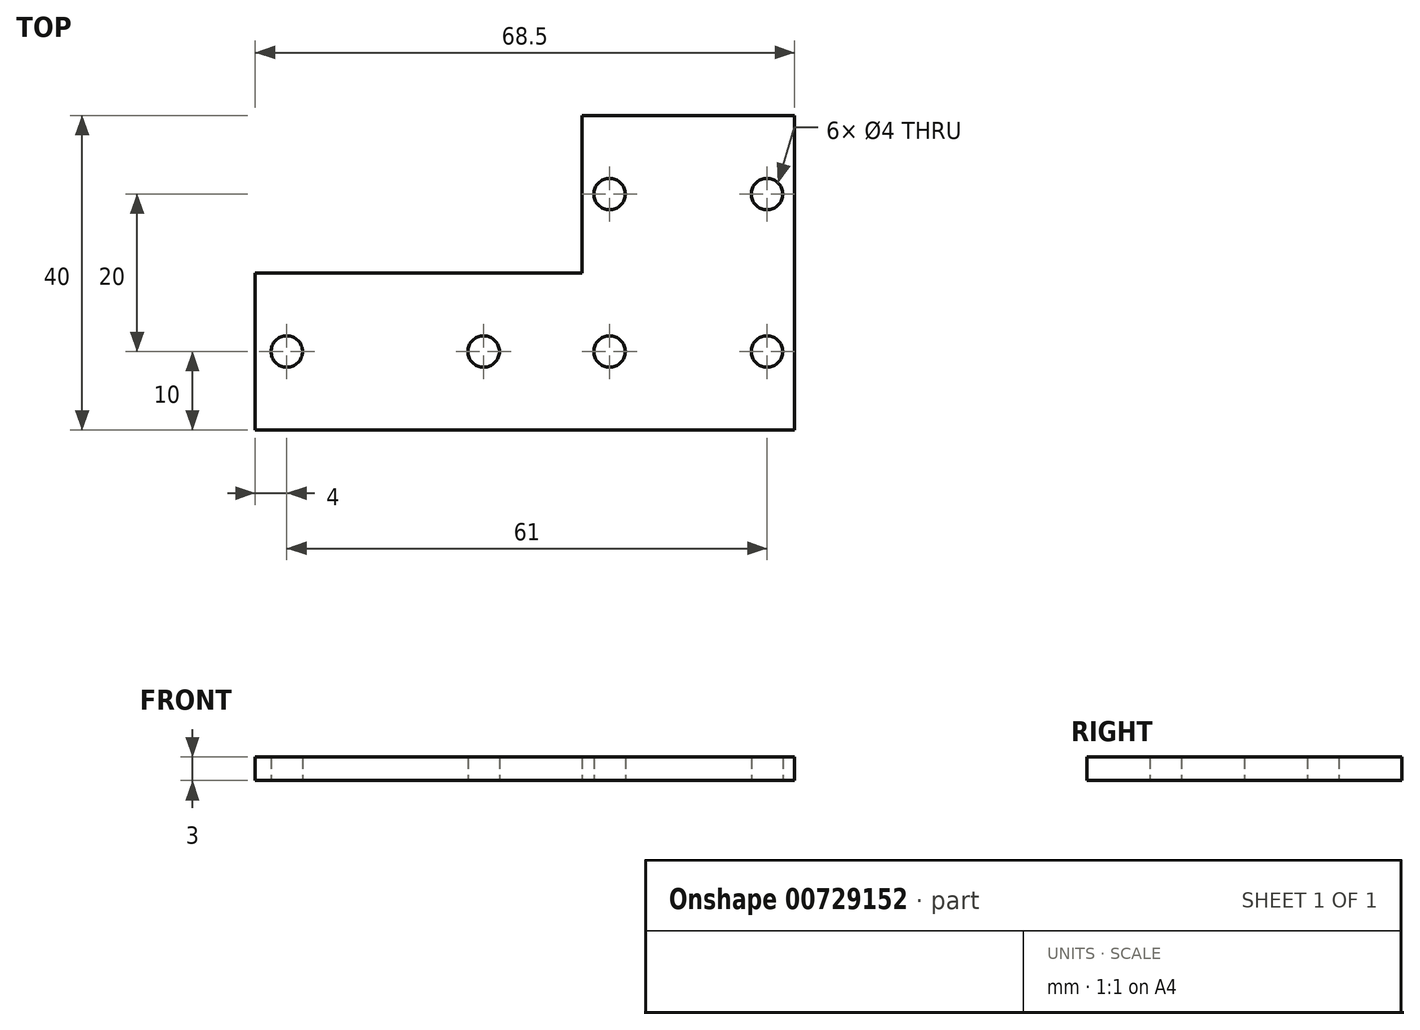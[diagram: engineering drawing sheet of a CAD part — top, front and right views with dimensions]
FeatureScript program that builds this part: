
annotation { "Feature Type Name" : "Feature", "Feature Type Description" : "" }
export const myFeature = defineFeature(function(context is Context, id is Id, definition is map)
    precondition{}
    {
        {
            var Q0;
            Q0=qCreatedBy(makeId("Top.planeOp"),FACE);
            var sketch = newSketch(context, id + "F0", { "sketchPlane" : qUnion([Q0])});
            skLineSegment(sketch, "E0.bottom", {"start": v(13.5, -20) * mm, "end": v(-55, -20) * mm});
            skLineSegment(sketch, "E0.top", {"start": v(13.5, 20) * mm, "end": v(-55, 20) * mm});
            skLineSegment(sketch, "E0.left", {"start": v(13.5, -20) * mm, "end": v(13.5, 20) * mm});
            skLineSegment(sketch, "E0.right", {"start": v(-55, -20) * mm, "end": v(-55, 20) * mm});
            skPoint(sketch, "E0.middle", {"position": v(0, 0) * mm});
            skLineSegment(sketch, "E1.bottom", {"start": v(10, -10) * mm, "end": v(-10, -10) * mm, "construction": true});
            skLineSegment(sketch, "E1.top", {"start": v(10, 10) * mm, "end": v(-10, 10) * mm, "construction": true});
            skLineSegment(sketch, "E1.left", {"start": v(10, -10) * mm, "end": v(10, 10) * mm, "construction": true});
            skLineSegment(sketch, "E1.right", {"start": v(-10, -10) * mm, "end": v(-10, 10) * mm, "construction": true});
            skLineSegment(sketch, "E2", {"start": v(0, 0) * mm, "end": v(0, 0) * mm});
            skPoint(sketch, "E3", {"position": v(-26, -10) * mm});
            skPoint(sketch, "E4", {"position": v(-51, -10) * mm});
            skLineSegment(sketch, "E5.bottom", {"start": v(-55, -20) * mm, "end": v(-13.5, -20) * mm});
            skLineSegment(sketch, "E5.left", {"start": v(-55, -20) * mm, "end": v(-55, -4.76) * mm});
            skLineSegment(sketch, "E6.bottom", {"start": v(-55, 20) * mm, "end": v(-13.5, 20) * mm});
            skLineSegment(sketch, "E6.top", {"start": v(-55, 0) * mm, "end": v(-13.5, 0) * mm});
            skLineSegment(sketch, "E6.left", {"start": v(-55, 20) * mm, "end": v(-55, 0) * mm});
            skLineSegment(sketch, "E6.right", {"start": v(-13.5, 20) * mm, "end": v(-13.5, 0) * mm});
            skSolve(sketch);
        }
        {
            var Q0;
            Q0=makeQuery(id+"F0.imprint","IMPRINT",FACE,{"disambiguationData":[TD([[makeQuery(id+"F0.imprint","IMPRINT",EDGE,{"derivedFrom":sQuery(id+"F0.wireOp",EDGE,"E0.bottom")}),-1.0]])]});
            extrude(context, id + "F1", {"entities" : qUnion([Q0]), "depth" : 3 * mm, "offsetDistance" : 25 * mm});
        }
        {
            var Q0;
            Q0=sQuery(id+"F0.wireOp",VERTEX,"E4");
            var Q1;
            Q1=sQuery(id+"F0.wireOp",VERTEX,"E3");
            var Q2;
            Q2=sQuery(id+"F0.wireOp",VERTEX,"E1.right.start");
            var Q3;
            Q3=sQuery(id+"F0.wireOp",VERTEX,"E1.top.start");
            var Q4;
            Q4=sQuery(id+"F0.wireOp",VERTEX,"E1.left.start");
            var Q5;
            Q5=sQuery(id+"F0.wireOp",VERTEX,"E1.top.end");
            var Q6;
            Q6=makeQuery(id+"F1.opExtrude","SWEPT_BODY",BODY,{"disambiguationData":[OSD([sQuery(id+"F0.wireOp",EDGE,"E0.bottom"),sQuery(id+"F0.wireOp",EDGE,"E0.top"),sQuery(id+"F0.wireOp",EDGE,"E0.left"),sQuery(id+"F0.wireOp",EDGE,"E0.right")])]});
            hole(context, id + "F2", {"style" : HoleStyle.SIMPLE, "endStyle" : HoleEndStyle.THROUGH, "oppositeDirection" : true, "holeDiameter" : 4 * mm, "majorDiameter" : 5 * mm, "isTappedThrough" : true, "tappedDepth" : 12 * mm, "tapClearance" : 3, "locations" : qUnion([Q0, Q1, Q2, Q3, Q4, Q5]), "scope" : qUnion([Q6])});
        }
    });
